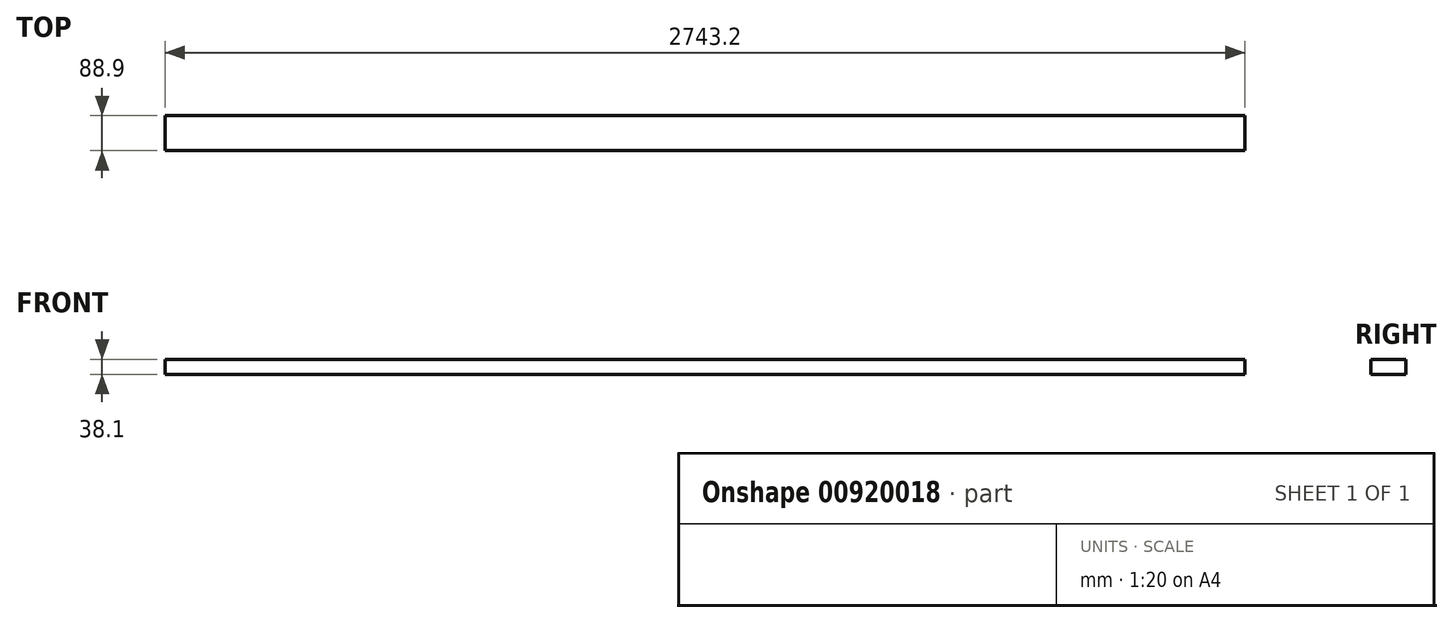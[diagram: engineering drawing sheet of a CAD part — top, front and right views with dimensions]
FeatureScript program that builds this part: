
annotation { "Feature Type Name" : "Feature", "Feature Type Description" : "" }
export const myFeature = defineFeature(function(context is Context, id is Id, definition is map)
    precondition{}
    {
        {
            var Q0;
            Q0=qCreatedBy(makeId("Right.planeOp"),FACE);
            var sketch = newSketch(context, id + "F0", { "sketchPlane" : qUnion([Q0])});
            skLineSegment(sketch, "E0.bottom", {"start": v(44.45, 19.05) * mm, "end": v(-44.45, 19.05) * mm});
            skLineSegment(sketch, "E0.top", {"start": v(44.45, -19.05) * mm, "end": v(-44.45, -19.05) * mm});
            skLineSegment(sketch, "E0.left", {"start": v(44.45, 19.05) * mm, "end": v(44.45, -19.05) * mm});
            skLineSegment(sketch, "E0.right", {"start": v(-44.45, 19.05) * mm, "end": v(-44.45, -19.05) * mm});
            skPoint(sketch, "E0.middle", {"position": v(0, 0) * mm});
            skSolve(sketch);
        }
        {
            var Q0;
            Q0 = qSketchRegion(id + "F0", true);
            extrude(context, id + "F1", {"entities" : qUnion([Q0]), "oppositeDirection" : true, "depth" : 2743.2 * mm, "offsetDistance" : 25.4 * mm});
        }
    });
